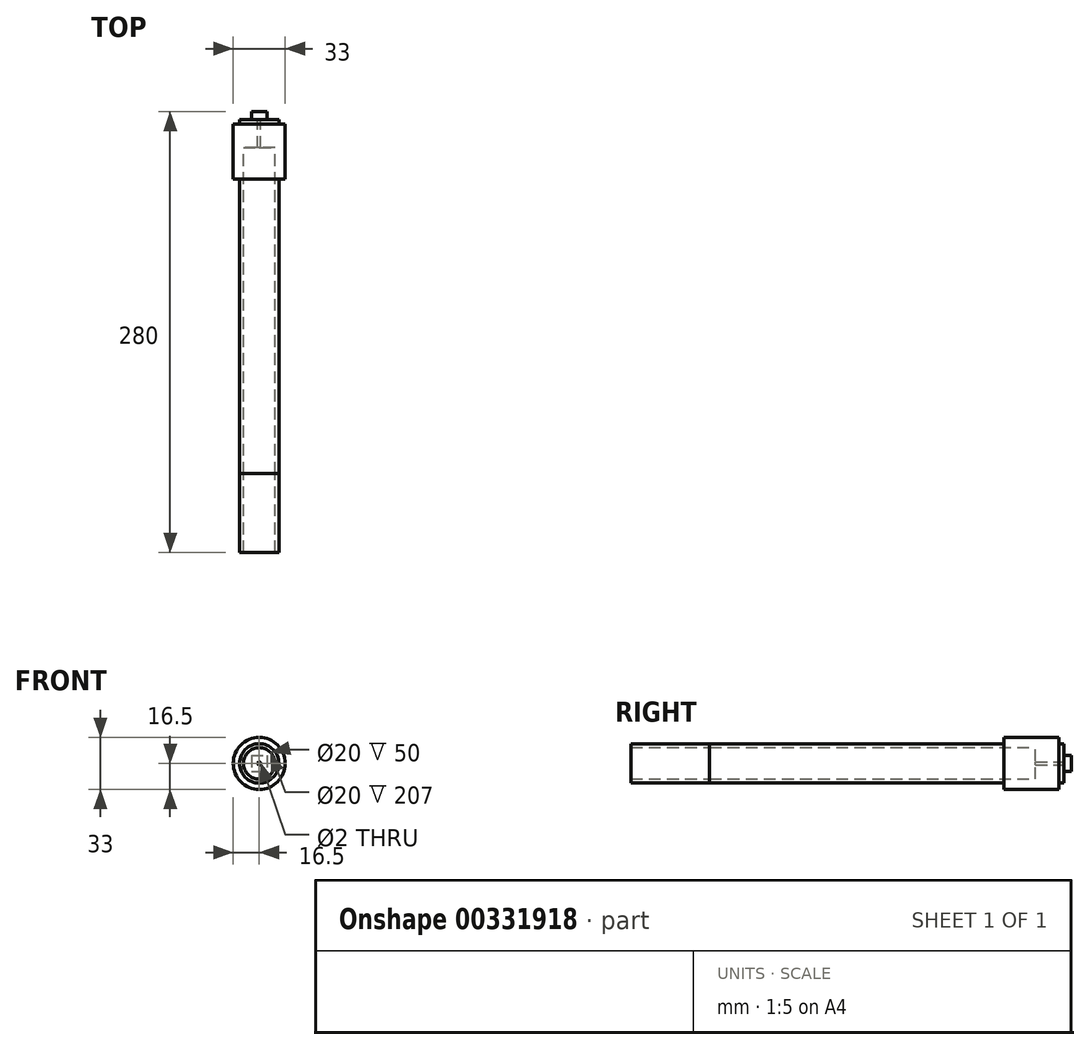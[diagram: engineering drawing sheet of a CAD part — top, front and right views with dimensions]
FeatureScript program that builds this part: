
annotation { "Feature Type Name" : "Feature", "Feature Type Description" : "" }
export const myFeature = defineFeature(function(context is Context, id is Id, definition is map)
    precondition{}
    {
        {
            var Q0;
            Q0=qCreatedBy(makeId("Front.planeOp"),FACE);
            var sketch = newSketch(context, id + "F0", { "sketchPlane" : qUnion([Q0])});
            skCircle(sketch, "E0", {"center": v(0, 0) * mm, "radius": 12.5 * mm});
            skCircle(sketch, "E1.0", {"center": v(0, 0) * mm, "radius": 10 * mm});
            skSolve(sketch);
        }
        {
            var Q0;
            Q0 = qSketchRegion(id + "F0", true);
            extrude(context, id + "F1", {"entities" : qUnion([Q0]), "depth" : 222 * mm});
        }
        {
            var Q0;
            Q0=makeQuery(id+"F1.opExtrude","CAP_FACE",FACE,{"disambiguationData":[OSD([sQuery(id+"F0.wireOp",EDGE,"E0"),sQuery(id+"F0.wireOp",EDGE,"E1.0")])],"isStart":false});
            extrude(context, id + "F2", {"entities" : qUnion([Q0]), "depth" : 50 * mm});
        }
        {
            var Q0;
            Q0=qCreatedBy(makeId("Front.planeOp"),FACE);
            var sketch = newSketch(context, id + "F3", { "sketchPlane" : qUnion([Q0])});
            skCircle(sketch, "E2.0", {"center": v(0, 0) * mm, "radius": 12.5 * mm});
            skCircle(sketch, "E3.0", {"center": v(0, 0) * mm, "radius": 16.5 * mm});
            skSolve(sketch);
        }
        {
            var Q0;
            Q0 = qSketchRegion(id + "F3", true);
            extrude(context, id + "F4", {"entities" : qUnion([Q0]), "depth" : 35 * mm});
        }
        {
            var Q0;
            Q0=qCreatedBy(makeId("Front.planeOp"),FACE);
            var sketch = newSketch(context, id + "F5", { "sketchPlane" : qUnion([Q0])});
            skCircle(sketch, "E4.0", {"center": v(0, 0) * mm, "radius": 10 * mm});
            skSolve(sketch);
        }
        {
            var Q0;
            Q0 = qSketchRegion(id + "F5", true);
            extrude(context, id + "F6", {"entities" : qUnion([Q0]), "depth" : 15 * mm});
        }
        {
            var Q0;
            Q0=makeQuery(id+"F6.opExtrude","CAP_FACE",FACE,{"disambiguationData":[OSD([sQuery(id+"F5.wireOp",EDGE,"E4.0")])],"isStart":true});
            var sketch = newSketch(context, id + "F7", { "sketchPlane" : qUnion([Q0])});
            skCircle(sketch, "E5", {"center": v(0, 0) * mm, "radius": 12.5 * mm});
            skSolve(sketch);
        }
        {
            var Q0;
            Q0 = qSketchRegion(id + "F7", true);
            extrude(context, id + "F8", {"entities" : qUnion([Q0]), "operationType" : NewBodyOperationType.ADD, "depth" : 3 * mm});
        }
        {
            var Q0;
            Q0=makeQuery(id+"F8.opExtrude","CAP_FACE",FACE,{"disambiguationData":[OSD([sQuery(id+"F7.wireOp",EDGE,"E5")])],"isStart":false});
            var sketch = newSketch(context, id + "F9", { "sketchPlane" : qUnion([Q0])});
            skLineSegment(sketch, "E6.bottom", {"start": v(5, 5) * mm, "end": v(-5, 5) * mm});
            skLineSegment(sketch, "E6.top", {"start": v(5, -5) * mm, "end": v(-5, -5) * mm});
            skLineSegment(sketch, "E6.left", {"start": v(5, 5) * mm, "end": v(5, -5) * mm});
            skLineSegment(sketch, "E6.right", {"start": v(-5, 5) * mm, "end": v(-5, -5) * mm});
            skPoint(sketch, "E6.middle", {"position": v(0, 0) * mm});
            skSolve(sketch);
        }
        {
            var Q0;
            Q0 = qSketchRegion(id + "F9", true);
            extrude(context, id + "F10", {"entities" : qUnion([Q0]), "operationType" : NewBodyOperationType.ADD, "depth" : 5 * mm});
        }
        {
            var Q0;
            Q0=makeQuery(id+"F10.opExtrude","CAP_FACE",FACE,{"disambiguationData":[OSD([sQuery(id+"F9.wireOp",EDGE,"E6.bottom"),sQuery(id+"F9.wireOp",EDGE,"E6.top"),sQuery(id+"F9.wireOp",EDGE,"E6.left"),sQuery(id+"F9.wireOp",EDGE,"E6.right")])],"isStart":false});
            var sketch = newSketch(context, id + "F11", { "sketchPlane" : qUnion([Q0])});
            skCircle(sketch, "E7", {"center": v(0, 0) * mm, "radius": 1 * mm});
            skSolve(sketch);
        }
        {
            var Q0;
            Q0 = qSketchRegion(id + "F11", true);
            extrude(context, id + "F12", {"entities" : qUnion([Q0]), "operationType" : NewBodyOperationType.REMOVE, "oppositeDirection" : true, "depth" : 25 * mm});
        }
    });
